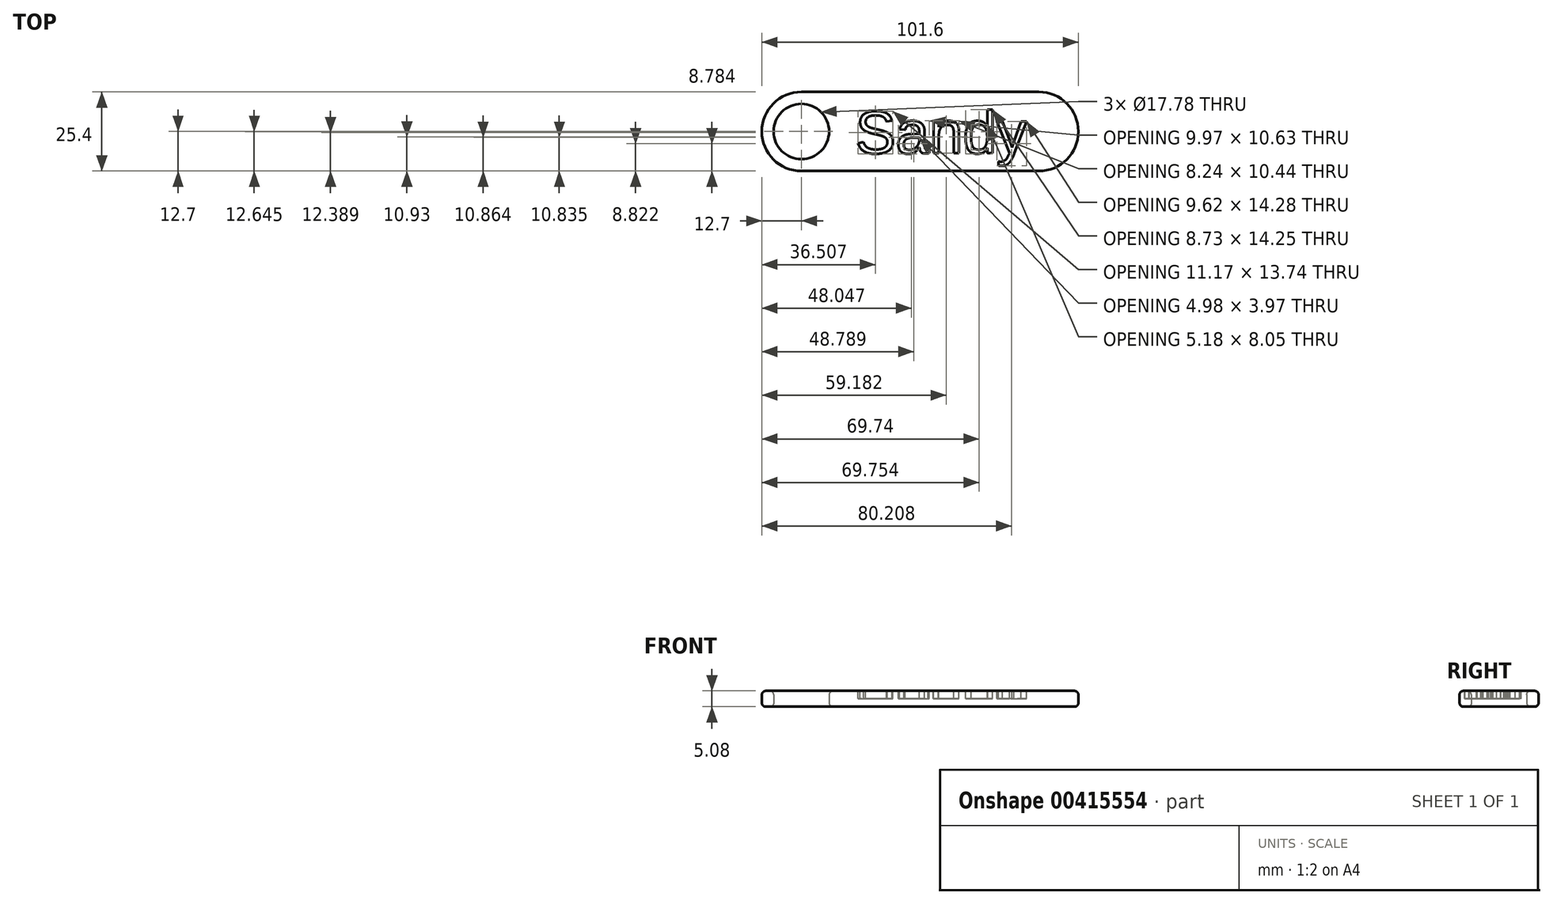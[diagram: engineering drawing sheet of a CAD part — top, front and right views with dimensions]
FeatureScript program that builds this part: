
annotation { "Feature Type Name" : "Feature", "Feature Type Description" : "" }
export const myFeature = defineFeature(function(context is Context, id is Id, definition is map)
    precondition{}
    {
        {
            var Q0;
            Q0=qCreatedBy(makeId("Top.planeOp"),FACE);
            var sketch = newSketch(context, id + "F0", { "sketchPlane" : qUnion([Q0])});
            skLineSegment(sketch, "E0.bottom", {"start": v(38.1, -12.7) * mm, "end": v(-38.1, -12.7) * mm});
            skLineSegment(sketch, "E0.top", {"start": v(38.1, 12.7) * mm, "end": v(-38.1, 12.7) * mm});
            skPoint(sketch, "E0.middle", {"position": v(0, 0) * mm});
            skArc(sketch, "E1", {"start": v(38.1, -12.7) * mm, "mid": v(50.8, 0) * mm, "end": v(38.1, 12.7) * mm});
            skArc(sketch, "E2", {"start": v(-38.1, 12.7) * mm, "mid": v(-50.8, 0) * mm, "end": v(-38.1, -12.7) * mm});
            skCircle(sketch, "E3", {"center": v(-38.1, 0) * mm, "radius": 8.9 * mm});
            skSolve(sketch);
        }
        {
            var Q0;
            Q0=makeQuery(id+"F0.imprint","IMPRINT",FACE,{"disambiguationData":[TD([[makeQuery(id+"F0.imprint","IMPRINT",EDGE,{"derivedFrom":sQuery(id+"F0.wireOp",EDGE,"E0.bottom")}),-1.0]])]});
            extrude(context, id + "F1", {"entities" : qUnion([Q0]), "depth" : 5.08 * mm});
        }
        {
            var Q0;
            Q0=makeQuery(id+"F1.opExtrude","CAP_FACE",FACE,{"disambiguationData":[OSD([sQuery(id+"F0.wireOp",EDGE,"E0.bottom"),sQuery(id+"F0.wireOp",EDGE,"E0.top"),sQuery(id+"F0.wireOp",EDGE,"E1"),sQuery(id+"F0.wireOp",EDGE,"E2"),sQuery(id+"F0.wireOp",EDGE,"E3")])],"isStart":false});
            var sketch = newSketch(context, id + "F2", { "sketchPlane" : qUnion([Q0])});
            skText(sketch, "E4", { "text": "Sandy", "fontName": "Arimo-Regular.ttf"});
            const initialGuessF2  = {"E4": [-0.02076, -0.00699, 1, 0, 0.01397]};
            skSetInitialGuess(sketch, initialGuessF2);
            skSolve(sketch);
        }
        {
            var Q0;
            Q0=qSketchRegion(id+"F2",true);
            extrude(context, id + "F3", {"entities" : qUnion([Q0]), "operationType" : NewBodyOperationType.REMOVE, "oppositeDirection" : true, "depth" : 2.54 * mm});
        }
        {
            var Q0;
            Q0=makeQuery(id+"F1.opExtrude","CAP_EDGE",EDGE,{"disambiguationData":[OSD([sQuery(id+"F0.wireOp",EDGE,"E2")])],"isStart":false});
            var Q1;
            Q1=makeQuery(id+"F1.opExtrude","CAP_FACE",FACE,{"disambiguationData":[OSD([sQuery(id+"F0.wireOp",EDGE,"E0.bottom"),sQuery(id+"F0.wireOp",EDGE,"E0.top"),sQuery(id+"F0.wireOp",EDGE,"E1"),sQuery(id+"F0.wireOp",EDGE,"E2"),sQuery(id+"F0.wireOp",EDGE,"E3")])],"isStart":true});
            var Q2;
            Q2=makeQuery(id+"F1.opExtrude","CAP_EDGE",EDGE,{"disambiguationData":[OSD([sQuery(id+"F0.wireOp",EDGE,"E3")])],"isStart":false});
            fillet(context, id + "F4", {"entities" : qUnion([Q0, Q1, Q2]), "radius" : 1.27 * mm, "tangentPropagation" : true, "allowEdgeOverflow" : false});
        }
    });
